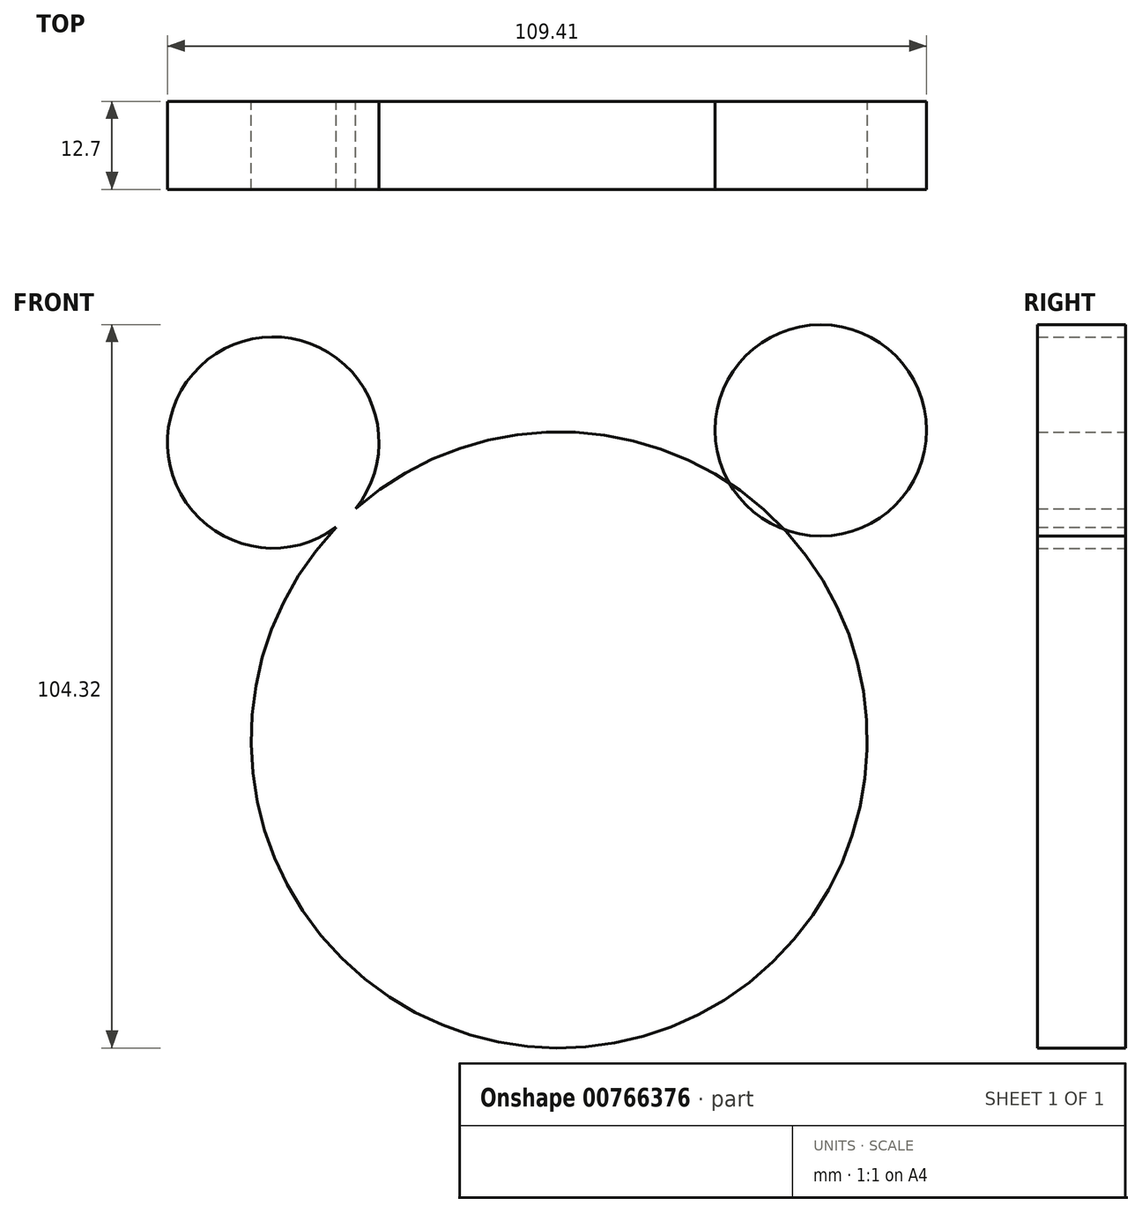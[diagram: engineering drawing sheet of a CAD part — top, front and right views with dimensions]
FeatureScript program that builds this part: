
annotation { "Feature Type Name" : "Feature", "Feature Type Description" : "" }
export const myFeature = defineFeature(function(context is Context, id is Id, definition is map)
    precondition{}
    {
        {
            var Q0;
            Q0=qCreatedBy(makeId("Front.planeOp"),FACE);
            var sketch = newSketch(context, id + "F0", { "sketchPlane" : qUnion([Q0])});
            skCircle(sketch, "E0", {"center": v(0, 0) * mm, "radius": 44.42 * mm});
            skSolve(sketch);
        }
        {
            var Q0;
            Q0=makeQuery(id+"F0.imprint","IMPRINT",FACE,{"disambiguationData":[TD([[makeQuery(id+"F0.imprint","IMPRINT",EDGE,{"derivedFrom":sQuery(id+"F0.wireOp",EDGE,"E0")}),1.0]])]});
            extrude(context, id + "F1", {"entities" : qUnion([Q0]), "depth" : 12.7 * mm, "offsetDistance" : 25.4 * mm});
        }
        {
            var Q0;
            Q0=qCreatedBy(makeId("Front.planeOp"),FACE);
            var sketch = newSketch(context, id + "F2", { "sketchPlane" : qUnion([Q0])});
            skCircle(sketch, "E1", {"center": v(-41.23, 42.9) * mm, "radius": 15.24 * mm});
            skSolve(sketch);
        }
        {
            var Q0;
            Q0=qCreatedBy(makeId("Front.planeOp"),FACE);
            var sketch = newSketch(context, id + "F3", { "sketchPlane" : qUnion([Q0])});
            skCircle(sketch, "E2", {"center": v(37.7, 44.66) * mm, "radius": 15.24 * mm});
            skSolve(sketch);
        }
        {
            var Q0;
            Q0=makeQuery(id+"F2.imprint","IMPRINT",FACE,{"disambiguationData":[TD([[makeQuery(id+"F2.imprint","IMPRINT",EDGE,{"derivedFrom":sQuery(id+"F2.wireOp",EDGE,"E1")}),1.0]])]});
            extrude(context, id + "F4", {"entities" : qUnion([Q0]), "operationType" : NewBodyOperationType.ADD, "depth" : 12.7 * mm, "offsetDistance" : 25.4 * mm});
        }
        {
            var Q0;
            Q0=makeQuery(id+"F3.imprint","IMPRINT",FACE,{"disambiguationData":[TD([[makeQuery(id+"F3.imprint","IMPRINT",EDGE,{"derivedFrom":sQuery(id+"F3.wireOp",EDGE,"E2")}),1.0]])]});
            extrude(context, id + "F5", {"entities" : qUnion([Q0]), "depth" : 12.7 * mm, "offsetDistance" : 25.4 * mm});
        }
    });
